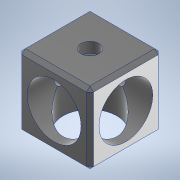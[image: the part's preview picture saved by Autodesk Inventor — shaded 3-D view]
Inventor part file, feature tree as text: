
AUTODESK INVENTOR PART (.ipt)
format: ipt  version: 2022 (Build 260153000, 153)  size: 158,720 bytes
history: imported  units: in
note: dims shown in document units (in); Inventor stores cm internally (conversion verified against a paired STEP export)
features: imported_body x1
ambient origin geometry x8: Origin, YZ Plane, XZ Plane, XY Plane, X Axis, Y Axis, Z Axis, Center Point
bodies: Solid1 (imported_parasolid), Body1 (imported_parasolid)
feature tree (1):
  imported_body  NMx_Import_Brep_tag  [imported B-rep: ~7 faces, bbox_mm=[0.0, 0.0, 0.0]]
